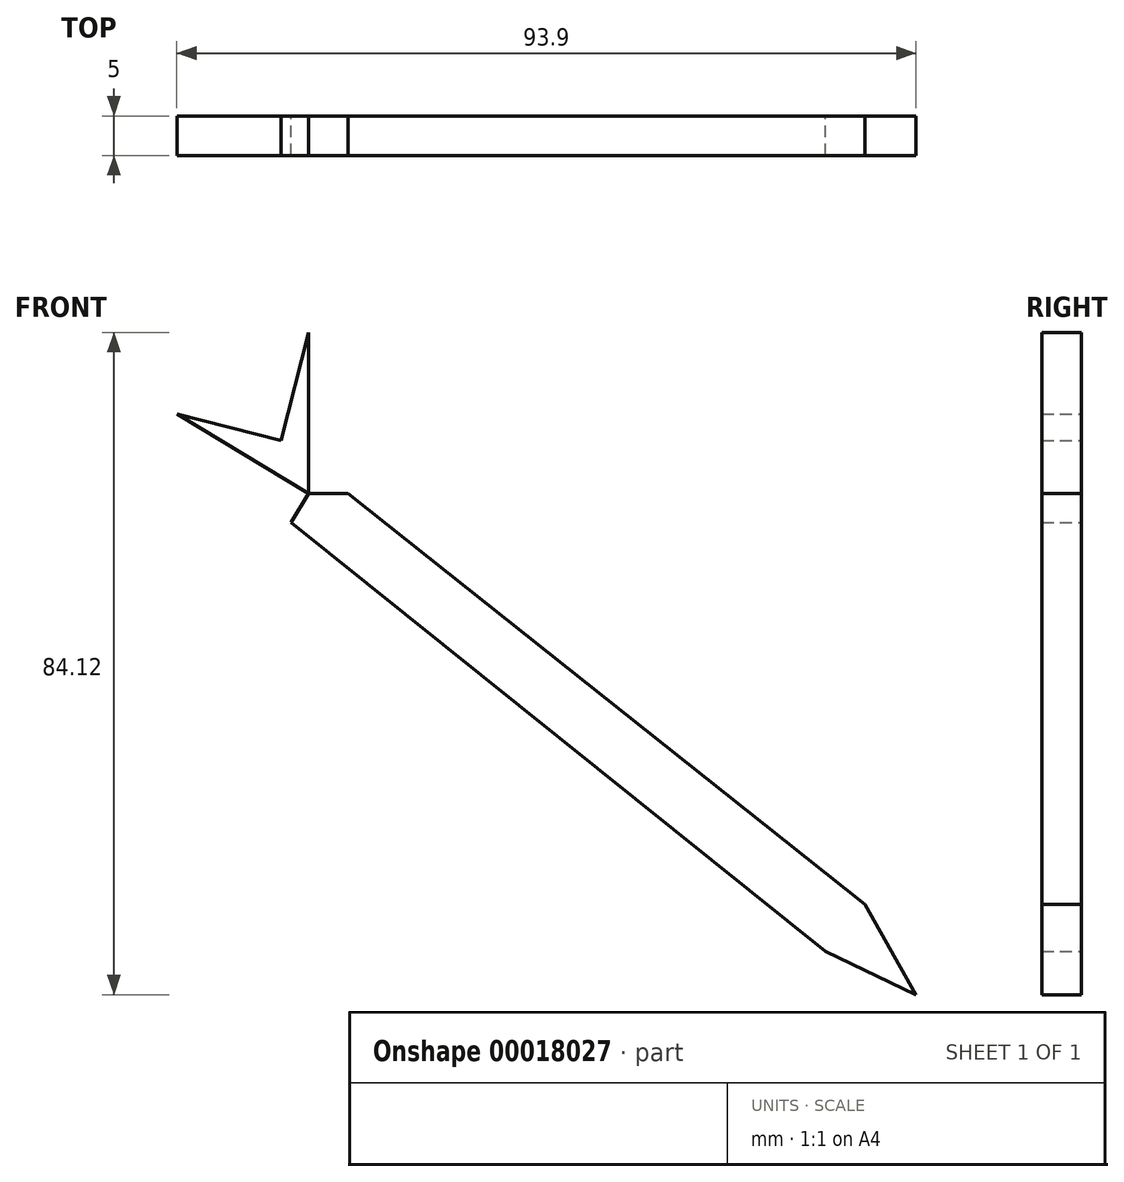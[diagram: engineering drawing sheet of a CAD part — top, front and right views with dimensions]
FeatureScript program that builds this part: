
annotation { "Feature Type Name" : "Feature", "Feature Type Description" : "" }
export const myFeature = defineFeature(function(context is Context, id is Id, definition is map)
    precondition{}
    {
        {
            var Q0;
            Q0=qCreatedBy(makeId("Front.planeOp"),FACE);
            var sketch = newSketch(context, id + "F0", { "sketchPlane" : qUnion([Q0])});
            skLineSegment(sketch, "E0", {"start": v(-41.2, 36.57) * mm, "end": v(-41.2, 48.8) * mm});
            skLineSegment(sketch, "E1", {"start": v(-41.2, 48.8) * mm, "end": v(-44.69, 35.07) * mm});
            skLineSegment(sketch, "E2", {"start": v(-44.69, 35.07) * mm, "end": v(-57.95, 38.45) * mm});
            skLineSegment(sketch, "E3", {"start": v(-57.95, 38.45) * mm, "end": v(-48.18, 32.58) * mm});
            skLineSegment(sketch, "E4", {"start": v(-48.18, 32.58) * mm, "end": v(-41.2, 28.38) * mm});
            skLineSegment(sketch, "E5", {"start": v(-41.2, 36.57) * mm, "end": v(-41.2, 28.38) * mm});
            skLineSegment(sketch, "E6", {"start": v(-41.2, 28.38) * mm, "end": v(-43.42, 24.67) * mm});
            skLineSegment(sketch, "E7", {"start": v(-41.2, 28.38) * mm, "end": v(-36.2, 28.38) * mm});
            skLineSegment(sketch, "E8", {"start": v(-36.2, 28.38) * mm, "end": v(29.46, -23.84) * mm});
            skLineSegment(sketch, "E9", {"start": v(-43.42, 24.67) * mm, "end": v(24.46, -29.83) * mm});
            skLineSegment(sketch, "E10", {"start": v(24.46, -29.83) * mm, "end": v(35.95, -35.32) * mm});
            skLineSegment(sketch, "E11", {"start": v(29.46, -23.84) * mm, "end": v(35.95, -35.32) * mm});
            skSolve(sketch);
        }
        {
            var Q0;
            Q0=makeQuery(id+"F0.imprint","IMPRINT",FACE,{"disambiguationData":[TD([[makeQuery(id+"F0.imprint","IMPRINT",EDGE,{"derivedFrom":sQuery(id+"F0.wireOp",EDGE,"E6")}),1.0]])]});
            var Q1;
            Q1=makeQuery(id+"F0.imprint","IMPRINT",FACE,{"disambiguationData":[TD([[makeQuery(id+"F0.imprint","IMPRINT",EDGE,{"derivedFrom":sQuery(id+"F0.wireOp",EDGE,"E0")}),1.0]])]});
            extrude(context, id + "F1", {"entities" : qUnion([Q0, Q1]), "depth" : 5 * mm});
        }
    });
